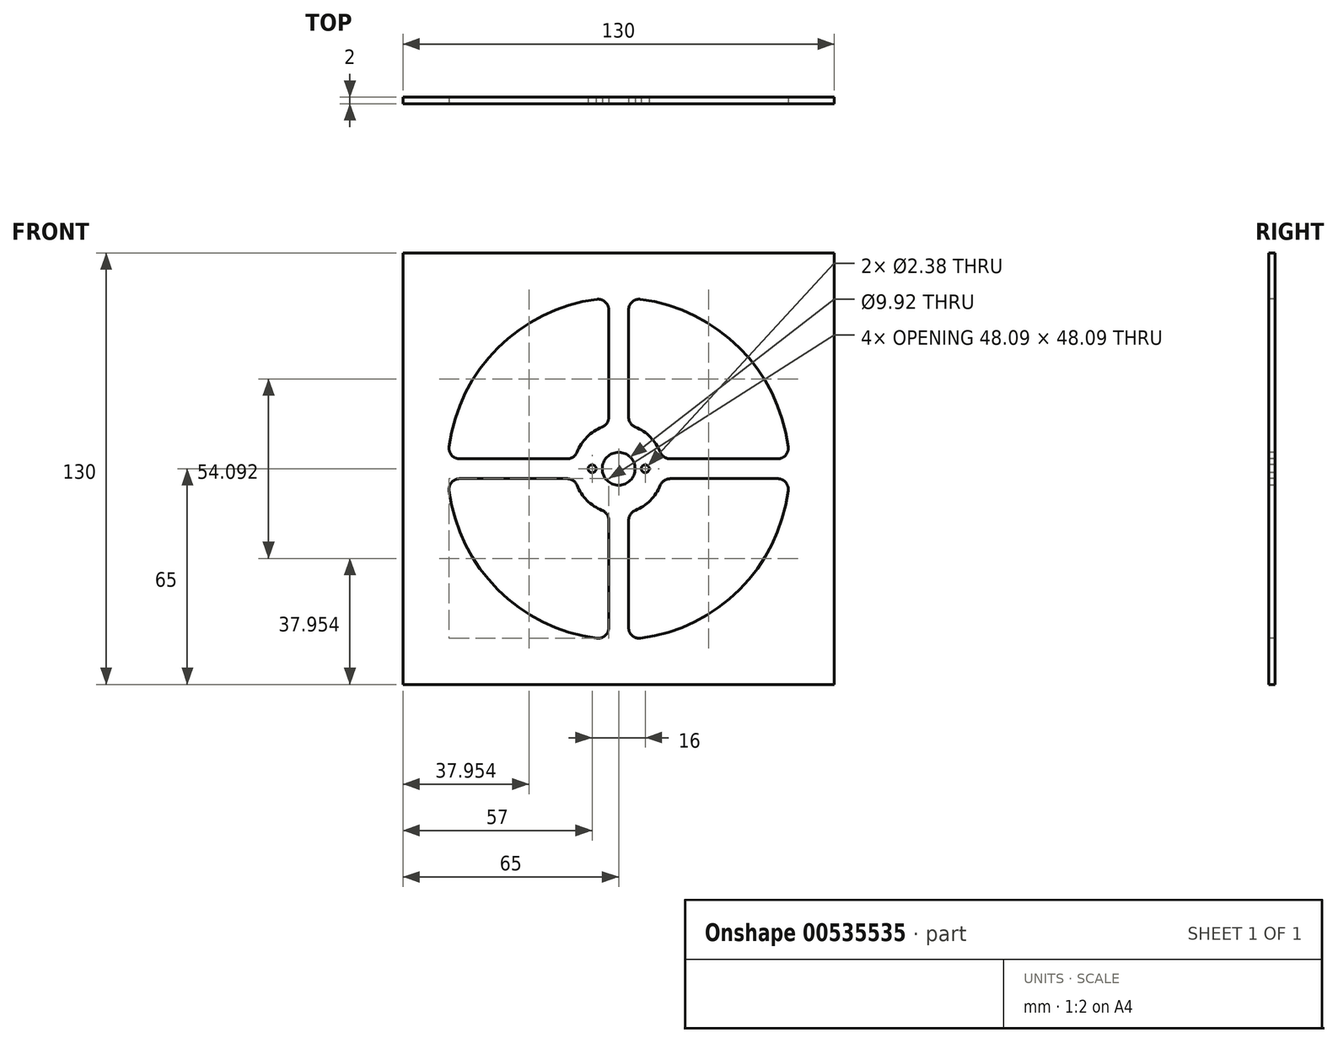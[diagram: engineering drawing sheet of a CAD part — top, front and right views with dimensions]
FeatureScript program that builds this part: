
annotation { "Feature Type Name" : "Feature", "Feature Type Description" : "" }
export const myFeature = defineFeature(function(context is Context, id is Id, definition is map)
    precondition{}
    {
        {
            var Q0;
            Q0=qCreatedBy(makeId("Front.planeOp"),FACE);
            var sketch = newSketch(context, id + "F0", { "sketchPlane" : qUnion([Q0])});
            skLineSegment(sketch, "E0", {"start": v(0, 65) * mm, "end": v(65, 65) * mm});
            skLineSegment(sketch, "E1", {"start": v(0, -65) * mm, "end": v(65, -65) * mm});
            skLineSegment(sketch, "E2", {"start": v(65, 65) * mm, "end": v(65, -65) * mm});
            skLineSegment(sketch, "E3.MirrorCS", {"start": v(-65, 65) * mm, "end": v(-65, -65) * mm});
            skLineSegment(sketch, "E4.MirrorCS", {"start": v(0, -65) * mm, "end": v(-65, -65) * mm});
            skLineSegment(sketch, "E5.MirrorCS", {"start": v(0, 65) * mm, "end": v(-65, 65) * mm});
            skSolve(sketch);
        }
        {
            var Q0;
            Q0 = qSketchRegion(id + "F0", true);
            extrude(context, id + "F1", {"entities" : qUnion([Q0]), "oppositeDirection" : true, "depth" : 2 * mm, "offsetDistance" : 25 * mm});
        }
        {
            var Q0;
            Q0=qCreatedBy(makeId("Front.planeOp"),FACE);
            var sketch = newSketch(context, id + "F2", { "sketchPlane" : qUnion([Q0])});
            skArc(sketch, "E6", {"start": v(-6.59, 51.08) * mm, "mid": v(-36.42, 36.42) * mm, "end": v(-51.08, 6.59) * mm});
            skArc(sketch, "E7", {"start": v(-5, 12.54) * mm, "mid": v(-9.55, 9.55) * mm, "end": v(-12.54, 5) * mm});
            skCircle(sketch, "E8", {"center": v(0, 0) * mm, "radius": 4.96 * mm});
            skLineSegment(sketch, "E9", {"start": v(-3, 47.92) * mm, "end": v(-3, 15.5) * mm});
            skLineSegment(sketch, "E10", {"start": v(3, 47.92) * mm, "end": v(3, 15.5) * mm});
            skLineSegment(sketch, "E11", {"start": v(-47.92, 3) * mm, "end": v(-15.5, 3) * mm});
            skLineSegment(sketch, "E12", {"start": v(-47.92, -3) * mm, "end": v(-15.5, -3) * mm});
            skArc(sketch, "E13.trimOffspring", {"start": v(12.54, 5) * mm, "mid": v(9.55, 9.55) * mm, "end": v(5, 12.54) * mm});
            skLineSegment(sketch, "E14.trimOffspring", {"start": v(-3, -15.5) * mm, "end": v(-3, -47.92) * mm});
            skLineSegment(sketch, "E15.trimOffspring", {"start": v(3, -15.5) * mm, "end": v(3, -47.92) * mm});
            skLineSegment(sketch, "E16.trimOffspring", {"start": v(15.5, -3) * mm, "end": v(47.92, -3) * mm});
            skLineSegment(sketch, "E17.trimOffspring", {"start": v(15.5, 3) * mm, "end": v(47.92, 3) * mm});
            skArc(sketch, "E18.trimOffspring", {"start": v(-12.54, -5) * mm, "mid": v(-9.55, -9.55) * mm, "end": v(-5, -12.54) * mm});
            skArc(sketch, "E19.trimOffspring", {"start": v(-51.08, -6.59) * mm, "mid": v(-36.42, -36.42) * mm, "end": v(-6.59, -51.08) * mm});
            skArc(sketch, "E20.trimOffspring", {"start": v(51.08, 6.59) * mm, "mid": v(36.42, 36.42) * mm, "end": v(6.59, 51.08) * mm});
            skArc(sketch, "E21.trimOffspring", {"start": v(5, -12.54) * mm, "mid": v(9.55, -9.55) * mm, "end": v(12.54, -5) * mm});
            skArc(sketch, "E22.trimOffspring", {"start": v(6.59, -51.08) * mm, "mid": v(36.42, -36.42) * mm, "end": v(51.08, -6.59) * mm});
            skPoint(sketch, "E23.visualSharp", {"position": v(-3, 13.16) * mm});
            skArc(sketch, "E23.filletArc", {"start": v(-5, 12.54) * mm, "mid": v(-3.55, 13.7) * mm, "end": v(-3, 15.5) * mm});
            skPoint(sketch, "E24.visualSharp", {"position": v(3, 13.16) * mm});
            skArc(sketch, "E24.filletArc", {"start": v(3, 15.5) * mm, "mid": v(3.55, 13.7) * mm, "end": v(5, 12.54) * mm});
            skPoint(sketch, "E25.visualSharp", {"position": v(51.41, 3) * mm});
            skArc(sketch, "E25.filletArc", {"start": v(47.92, 3) * mm, "mid": v(50.31, 4.08) * mm, "end": v(51.08, 6.59) * mm});
            skPoint(sketch, "E26.visualSharp", {"position": v(51.41, -3) * mm});
            skArc(sketch, "E26.filletArc", {"start": v(51.08, -6.59) * mm, "mid": v(50.31, -4.08) * mm, "end": v(47.92, -3) * mm});
            skPoint(sketch, "E27.visualSharp", {"position": v(3, 51.41) * mm});
            skArc(sketch, "E27.filletArc", {"start": v(6.59, 51.08) * mm, "mid": v(4.08, 50.31) * mm, "end": v(3, 47.92) * mm});
            skPoint(sketch, "E28.visualSharp", {"position": v(-3, 51.41) * mm});
            skArc(sketch, "E28.filletArc", {"start": v(-3, 47.92) * mm, "mid": v(-4.08, 50.31) * mm, "end": v(-6.59, 51.08) * mm});
            skPoint(sketch, "E29.visualSharp", {"position": v(-51.41, 3) * mm});
            skArc(sketch, "E29.filletArc", {"start": v(-51.08, 6.59) * mm, "mid": v(-50.31, 4.08) * mm, "end": v(-47.92, 3) * mm});
            skPoint(sketch, "E30.visualSharp", {"position": v(-51.41, -3) * mm});
            skArc(sketch, "E30.filletArc", {"start": v(-47.92, -3) * mm, "mid": v(-50.31, -4.08) * mm, "end": v(-51.08, -6.59) * mm});
            skPoint(sketch, "E31.visualSharp", {"position": v(-13.16, -3) * mm});
            skArc(sketch, "E31.filletArc", {"start": v(-12.54, -5) * mm, "mid": v(-13.7, -3.55) * mm, "end": v(-15.5, -3) * mm});
            skPoint(sketch, "E32.visualSharp", {"position": v(-3, -13.16) * mm});
            skArc(sketch, "E32.filletArc", {"start": v(-3, -15.5) * mm, "mid": v(-3.55, -13.7) * mm, "end": v(-5, -12.54) * mm});
            skPoint(sketch, "E33.visualSharp", {"position": v(3, -13.16) * mm});
            skArc(sketch, "E33.filletArc", {"start": v(5, -12.54) * mm, "mid": v(3.55, -13.7) * mm, "end": v(3, -15.5) * mm});
            skPoint(sketch, "E34.visualSharp", {"position": v(13.16, -3) * mm});
            skArc(sketch, "E34.filletArc", {"start": v(15.5, -3) * mm, "mid": v(13.7, -3.55) * mm, "end": v(12.54, -5) * mm});
            skPoint(sketch, "E35.visualSharp", {"position": v(13.16, 3) * mm});
            skArc(sketch, "E35.filletArc", {"start": v(12.54, 5) * mm, "mid": v(13.7, 3.55) * mm, "end": v(15.5, 3) * mm});
            skPoint(sketch, "E36.visualSharp", {"position": v(-13.16, 3) * mm});
            skArc(sketch, "E36.filletArc", {"start": v(-15.5, 3) * mm, "mid": v(-13.7, 3.55) * mm, "end": v(-12.54, 5) * mm});
            skCircle(sketch, "E37", {"center": v(8, 0) * mm, "radius": 1.2 * mm});
            skCircle(sketch, "E38", {"center": v(-8, 0) * mm, "radius": 1.2 * mm});
            skPoint(sketch, "E39.newPointA", {"position": v(-3, -62.04) * mm});
            skArc(sketch, "E39.filletArc", {"start": v(-6.59, -51.08) * mm, "mid": v(-4.08, -50.31) * mm, "end": v(-3, -47.92) * mm});
            skPoint(sketch, "E40.newPointA", {"position": v(3, -62.04) * mm});
            skArc(sketch, "E40.filletArc", {"start": v(3, -47.92) * mm, "mid": v(4.08, -50.31) * mm, "end": v(6.59, -51.08) * mm});
            skSolve(sketch);
        }
        {
            var Q0;
            Q0=makeQuery(id+"F2.imprint","IMPRINT",FACE,{"disambiguationData":[TD([[makeQuery(id+"F2.imprint","IMPRINT",EDGE,{"derivedFrom":sQuery(id+"F2.wireOp",EDGE,"E6")}),1.0]])]});
            var Q1;
            Q1=makeQuery(id+"F2.imprint","IMPRINT",FACE,{"disambiguationData":[TD([[makeQuery(id+"F2.imprint","IMPRINT",EDGE,{"derivedFrom":sQuery(id+"F2.wireOp",EDGE,"E10")}),1.0]])]});
            var Q2;
            Q2=makeQuery(id+"F2.imprint","IMPRINT",FACE,{"disambiguationData":[TD([[makeQuery(id+"F2.imprint","IMPRINT",EDGE,{"derivedFrom":sQuery(id+"F2.wireOp",EDGE,"E12")}),-1.0]])]});
            var Q3;
            Q3=makeQuery(id+"F2.imprint","IMPRINT",FACE,{"disambiguationData":[TD([[makeQuery(id+"F2.imprint","IMPRINT",EDGE,{"derivedFrom":sQuery(id+"F2.wireOp",EDGE,"E15.trimOffspring")}),1.0]])]});
            var Q4;
            Q4=makeQuery(id+"F2.imprint","IMPRINT",FACE,{"disambiguationData":[TD([[makeQuery(id+"F2.imprint","IMPRINT",EDGE,{"derivedFrom":sQuery(id+"F2.wireOp",EDGE,"E38")}),1.0]])]});
            var Q5;
            Q5=makeQuery(id+"F2.imprint","IMPRINT",FACE,{"disambiguationData":[TD([[makeQuery(id+"F2.imprint","IMPRINT",EDGE,{"derivedFrom":sQuery(id+"F2.wireOp",EDGE,"E37")}),1.0]])]});
            var Q6;
            Q6=makeQuery(id+"F2.imprint","IMPRINT",FACE,{"disambiguationData":[TD([[makeQuery(id+"F2.imprint","IMPRINT",EDGE,{"derivedFrom":sQuery(id+"F2.wireOp",EDGE,"E8")}),1.0]])]});
            extrude(context, id + "F3", {"entities" : qUnion([Q0, Q1, Q2, Q3, Q4, Q5, Q6]), "operationType" : NewBodyOperationType.REMOVE, "endBound" : BoundingType.THROUGH_ALL, "oppositeDirection" : true, "depth" : 25 * mm, "offsetDistance" : 25 * mm});
        }
    });
